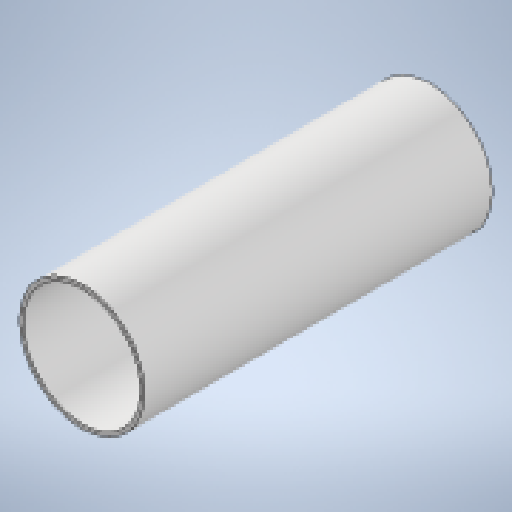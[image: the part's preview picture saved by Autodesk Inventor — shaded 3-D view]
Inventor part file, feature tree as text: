
AUTODESK INVENTOR PART (.ipt)
format: ipt  version: 2025.1 (Build 291241020, 241B)  size: 142,848 bytes
history: native  units: mm
features: extrude x1, sketch x1
ambient origin geometry x8: Origin, YZ Plane, XZ Plane, XY Plane, X Axis, Y Axis, Z Axis, Center Point
bodies: Solid1 (feature_tree)
feature tree (2):
  extrude  "Extrusion1"  Depth=250.0mm
  sketch  "Sketch1"  dims[d0=90.0mm d1=3.0mm d2=250.0mm d3=0.0mm]
